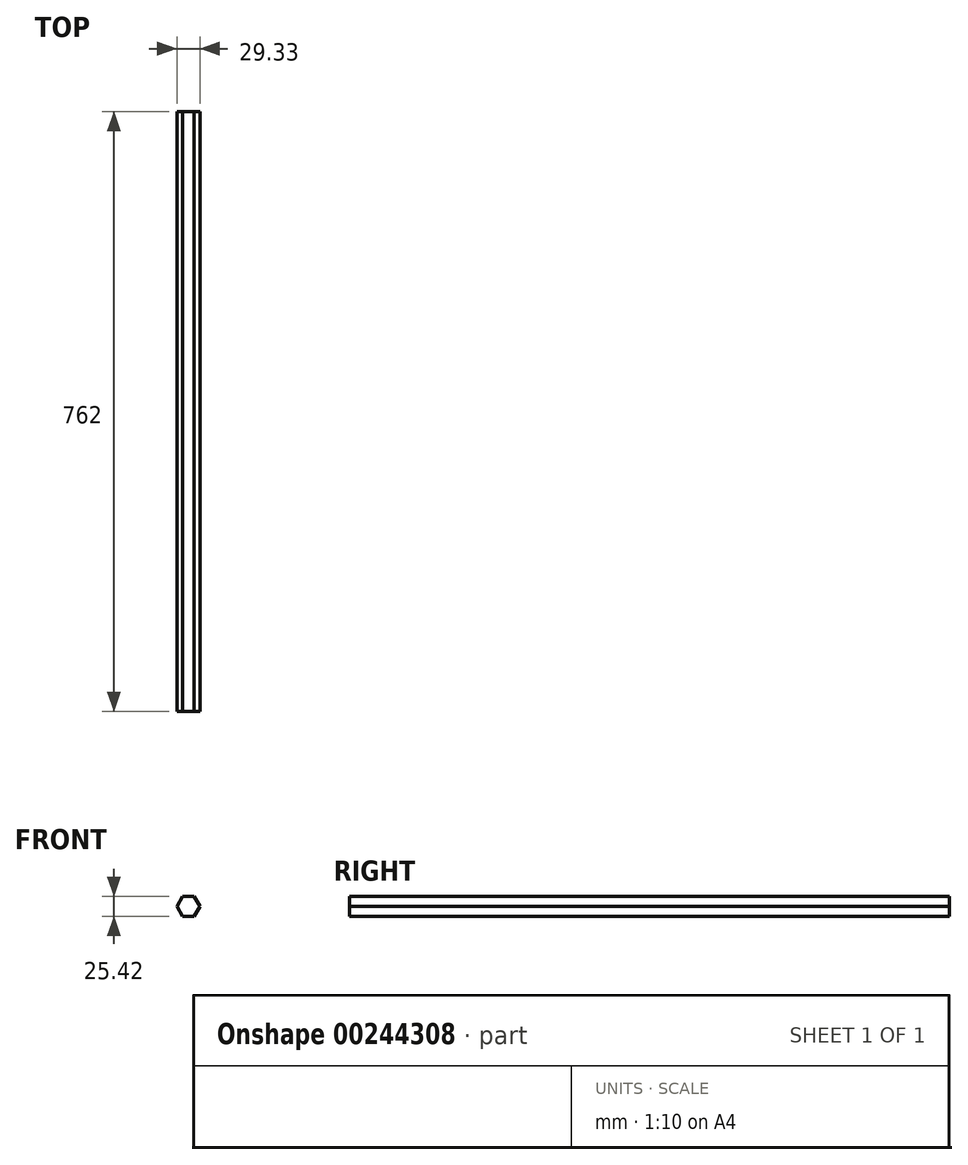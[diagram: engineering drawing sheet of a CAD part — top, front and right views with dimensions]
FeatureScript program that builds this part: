
annotation { "Feature Type Name" : "Feature", "Feature Type Description" : "" }
export const myFeature = defineFeature(function(context is Context, id is Id, definition is map)
    precondition{}
    {
        {
            var Q0;
            Q0=qCreatedBy(makeId("Front.planeOp"),FACE);
            var sketch = newSketch(context, id + "F0", { "sketchPlane" : qUnion([Q0])});
            skCircle(sketch, "E0", {"center": v(1.08, 0) * mm, "radius": 12.7 * mm});
            skCircle(sketch, "E1.cCircle", {"center": v(1.08, 0) * mm, "radius": 12.7 * mm, "construction": true});
            skLineSegment(sketch, "E1.0", {"start": v(15.74, -0.03) * mm, "end": v(8.39, -12.71) * mm});
            skLineSegment(sketch, "E1.1", {"start": v(8.39, -12.71) * mm, "end": v(-6.28, -12.69) * mm});
            skLineSegment(sketch, "E1.2", {"start": v(-6.28, -12.69) * mm, "end": v(-13.59, 0.03) * mm});
            skLineSegment(sketch, "E1.3", {"start": v(-13.59, 0.03) * mm, "end": v(-6.23, 12.71) * mm});
            skLineSegment(sketch, "E1.4", {"start": v(-6.23, 12.71) * mm, "end": v(8.44, 12.69) * mm});
            skLineSegment(sketch, "E1.5", {"start": v(8.44, 12.69) * mm, "end": v(15.74, -0.03) * mm});
            skPoint(sketch, "E1.0.midPoint", {"position": v(12.07, -6.37) * mm});
            skSolve(sketch);
        }
        {
            var Q0;
            Q0 = qSketchRegion(id + "F0", true);
            extrude(context, id + "F1", {"entities" : qUnion([Q0]), "depth" : 762 * mm});
        }
    });
